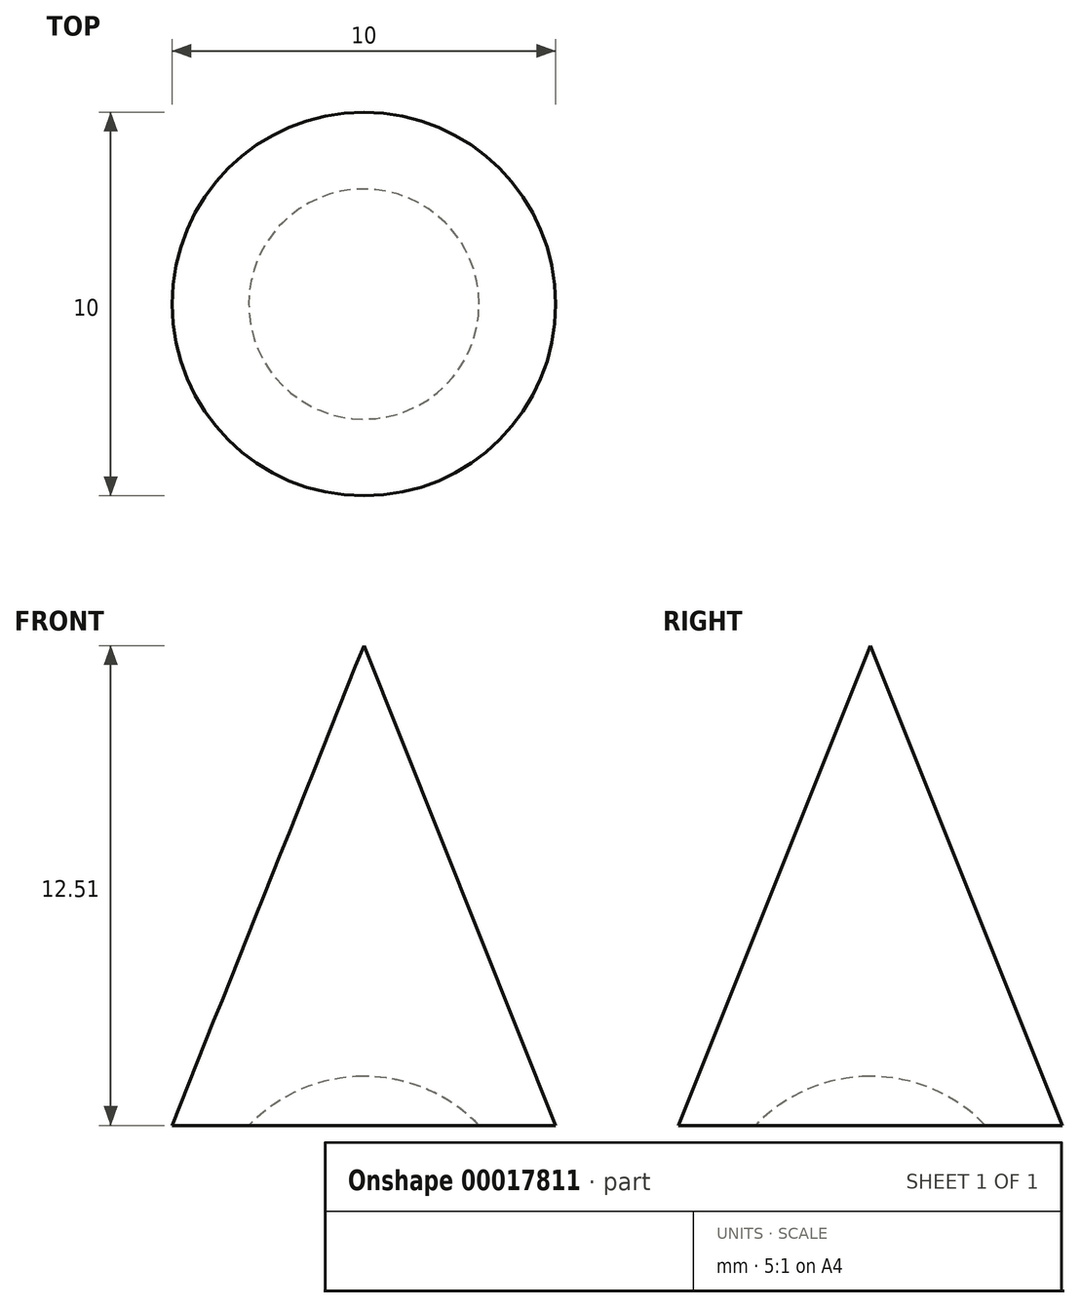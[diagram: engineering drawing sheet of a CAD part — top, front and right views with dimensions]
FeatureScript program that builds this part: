
annotation { "Feature Type Name" : "Feature", "Feature Type Description" : "" }
export const myFeature = defineFeature(function(context is Context, id is Id, definition is map)
    precondition{}
    {
        {
            var Q0;
            Q0=qCreatedBy(makeId("Front.planeOp"),FACE);
            var sketch = newSketch(context, id + "F0", { "sketchPlane" : qUnion([Q0])});
            skLineSegment(sketch, "E0", {"start": v(0, 12.5) * mm, "end": v(5, 0) * mm});
            skLineSegment(sketch, "E1", {"start": v(0, 12.5) * mm, "end": v(0, 1.28) * mm});
            skArc(sketch, "E2", {"start": v(3, 0) * mm, "mid": v(1.63, 0.94) * mm, "end": v(0, 1.28) * mm});
            skLineSegment(sketch, "E3", {"start": v(5, 0) * mm, "end": v(3, 0) * mm});
            skSolve(sketch);
        }
        {
            var Q0;
            Q0=makeQuery(id+"F0.imprint","IMPRINT",FACE,{"disambiguationData":[TD([[makeQuery(id+"F0.imprint","IMPRINT",EDGE,{"derivedFrom":sQuery(id+"F0.wireOp",EDGE,"E0")}),-1.0]])]});
            var Q1;
            Q1=sQuery(id+"F0.wireOp",EDGE,"E1");
            revolve(context, id + "F1", {"entities" : qUnion([Q0]), "axis" : qUnion([Q1]), "revolveType" : RevolveType.FULL});
        }
    });
